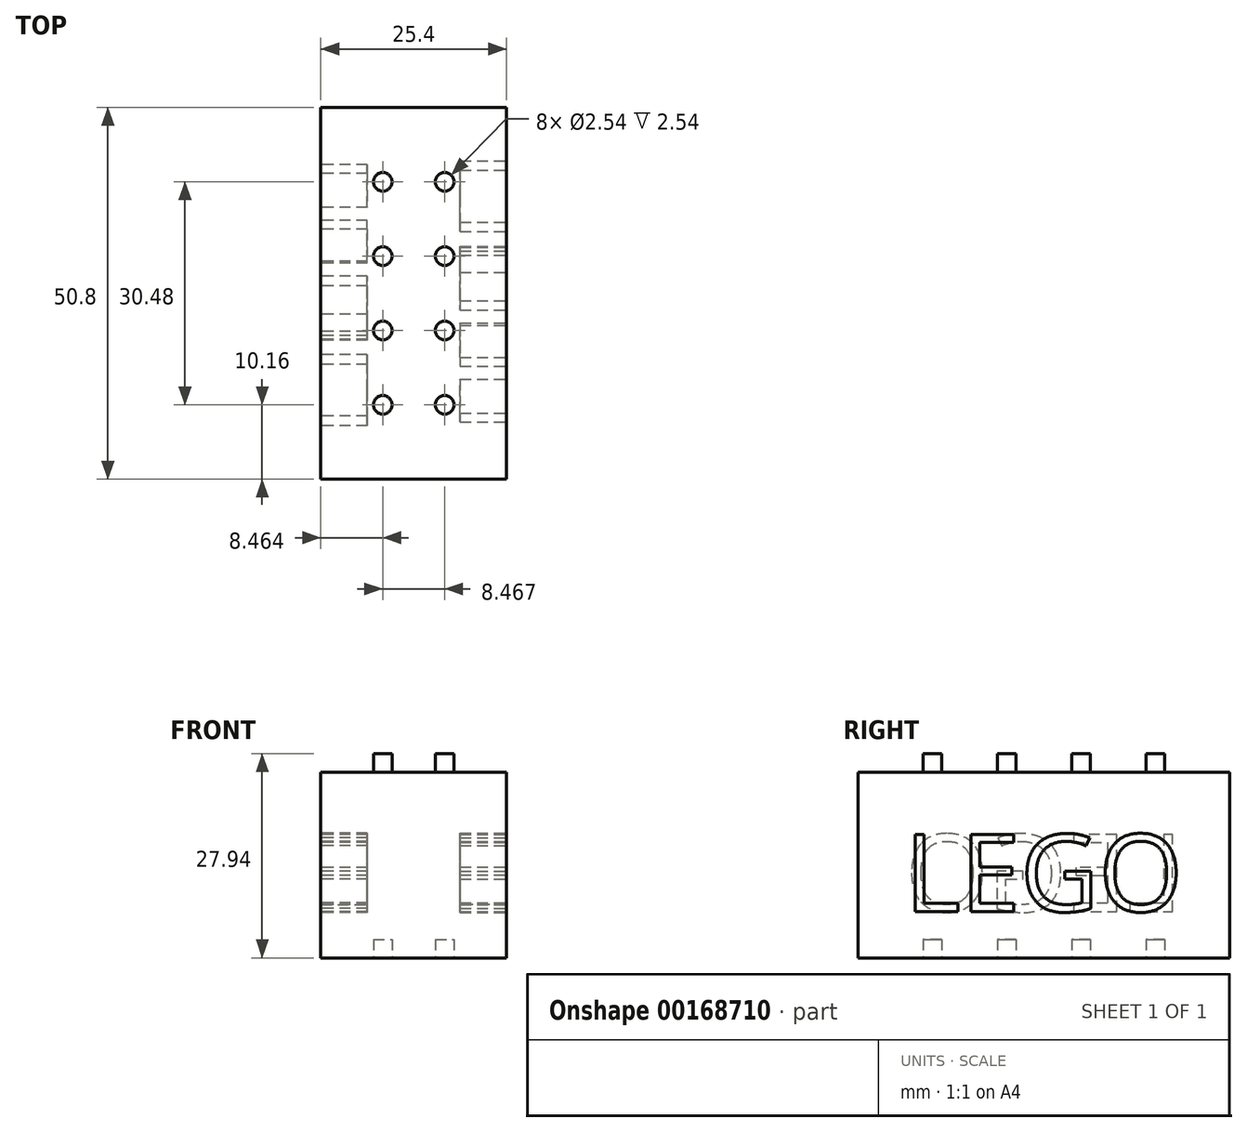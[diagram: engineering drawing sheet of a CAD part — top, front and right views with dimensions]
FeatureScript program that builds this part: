
annotation { "Feature Type Name" : "Feature", "Feature Type Description" : "" }
export const myFeature = defineFeature(function(context is Context, id is Id, definition is map)
    precondition{}
    {
        {
            var Q0;
            Q0=qCreatedBy(makeId("Top.planeOp"),FACE);
            var sketch = newSketch(context, id + "F0", { "sketchPlane" : qUnion([Q0])});
            skLineSegment(sketch, "E0.bottom", {"start": v(12.7, -25.4) * mm, "end": v(-12.7, -25.4) * mm});
            skLineSegment(sketch, "E0.top", {"start": v(12.7, 25.4) * mm, "end": v(-12.7, 25.4) * mm});
            skLineSegment(sketch, "E0.right", {"start": v(-12.7, -25.4) * mm, "end": v(-12.7, 25.4) * mm});
            skLineSegment(sketch, "E1", {"start": v(12.7, 25.4) * mm, "end": v(12.7, -25.4) * mm});
            skSolve(sketch);
        }
        {
            var Q0;
            Q0 = qSketchRegion(id + "F0", true);
            extrude(context, id + "F1", {"entities" : qUnion([Q0]), "depth" : 25.4 * mm});
        }
        {
            var Q0;
            Q0=makeQuery(id+"F1.opExtrude","CAP_FACE",FACE,{"disambiguationData":[OSD([sQuery(id+"F0.wireOp",EDGE,"E0.bottom"),sQuery(id+"F0.wireOp",EDGE,"E0.top"),sQuery(id+"F0.wireOp",EDGE,"E0.right"),sQuery(id+"F0.wireOp",EDGE,"E1")])],"isStart":true});
            var sketch = newSketch(context, id + "F2", { "sketchPlane" : qUnion([Q0])});
            skLineSegment(sketch, "E2", {"start": v(-12.7, 15.24) * mm, "end": v(12.7, 15.24) * mm, "construction": true});
            skLineSegment(sketch, "E3", {"start": v(-12.7, 5.08) * mm, "end": v(12.7, 5.08) * mm, "construction": true});
            skLineSegment(sketch, "E4", {"start": v(-12.7, -5.08) * mm, "end": v(12.7, -5.08) * mm, "construction": true});
            skLineSegment(sketch, "E5", {"start": v(-12.7, -15.24) * mm, "end": v(12.7, -15.24) * mm, "construction": true});
            skLineSegment(sketch, "E6", {"start": v(-4.24, 25.4) * mm, "end": v(-4.24, -25.4) * mm, "construction": true});
            skLineSegment(sketch, "E7", {"start": v(4.23, 25.4) * mm, "end": v(4.23, -25.4) * mm, "construction": true});
            skCircle(sketch, "E8", {"center": v(-4.24, 15.24) * mm, "radius": 1.27 * mm});
            skCircle(sketch, "E9", {"center": v(4.23, 15.24) * mm, "radius": 1.27 * mm});
            skCircle(sketch, "E10", {"center": v(-4.24, 5.08) * mm, "radius": 1.27 * mm});
            skCircle(sketch, "E11", {"center": v(4.23, 5.08) * mm, "radius": 1.27 * mm});
            skCircle(sketch, "E12", {"center": v(-4.24, -5.08) * mm, "radius": 1.27 * mm});
            skCircle(sketch, "E13", {"center": v(4.23, -5.08) * mm, "radius": 1.27 * mm});
            skCircle(sketch, "E14", {"center": v(-4.24, -15.24) * mm, "radius": 1.27 * mm});
            skCircle(sketch, "E15", {"center": v(4.23, -15.24) * mm, "radius": 1.27 * mm});
            skSolve(sketch);
        }
        {
            var Q0;
            Q0 = qSketchRegion(id + "F2", true);
            extrude(context, id + "F3", {"entities" : qUnion([Q0]), "operationType" : NewBodyOperationType.REMOVE, "oppositeDirection" : true, "depth" : 2.54 * mm});
        }
        {
            var Q0;
            Q0=makeQuery(id+"F1.opExtrude","CAP_FACE",FACE,{"disambiguationData":[OSD([sQuery(id+"F0.wireOp",EDGE,"E0.bottom"),sQuery(id+"F0.wireOp",EDGE,"E0.top"),sQuery(id+"F0.wireOp",EDGE,"E0.right"),sQuery(id+"F0.wireOp",EDGE,"E1")])],"isStart":false});
            var sketch = newSketch(context, id + "F4", { "sketchPlane" : qUnion([Q0])});
            skLineSegment(sketch, "E16", {"start": v(-12.79, 15.24) * mm, "end": v(12.61, 15.24) * mm, "construction": true});
            skLineSegment(sketch, "E17", {"start": v(-12.7, 5.08) * mm, "end": v(12.7, 5.08) * mm, "construction": true});
            skLineSegment(sketch, "E18", {"start": v(-12.7, -5.08) * mm, "end": v(12.7, -5.08) * mm, "construction": true});
            skLineSegment(sketch, "E19", {"start": v(-12.7, -15.24) * mm, "end": v(12.7, -15.24) * mm, "construction": true});
            skLineSegment(sketch, "E20", {"start": v(-4.23, 25.4) * mm, "end": v(-4.23, -25.4) * mm, "construction": true});
            skLineSegment(sketch, "E21", {"start": v(4.23, 25.4) * mm, "end": v(4.23, -25.4) * mm, "construction": true});
            skCircle(sketch, "E22", {"center": v(-4.23, 15.24) * mm, "radius": 1.27 * mm});
            skCircle(sketch, "E23", {"center": v(4.23, 15.24) * mm, "radius": 1.27 * mm});
            skCircle(sketch, "E24", {"center": v(-4.23, 5.08) * mm, "radius": 1.27 * mm});
            skCircle(sketch, "E25", {"center": v(4.23, 5.08) * mm, "radius": 1.27 * mm});
            skCircle(sketch, "E26", {"center": v(-4.23, -5.08) * mm, "radius": 1.27 * mm});
            skCircle(sketch, "E27", {"center": v(4.23, -5.08) * mm, "radius": 1.27 * mm});
            skCircle(sketch, "E28", {"center": v(-4.23, -15.24) * mm, "radius": 1.27 * mm});
            skCircle(sketch, "E29", {"center": v(4.23, -15.24) * mm, "radius": 1.27 * mm});
            skSolve(sketch);
        }
        {
            var Q0;
            Q0 = qSketchRegion(id + "F4", true);
            extrude(context, id + "F5", {"entities" : qUnion([Q0]), "operationType" : NewBodyOperationType.ADD, "depth" : 2.54 * mm});
        }
        {
            var Q0;
            Q0=makeQuery(id+"F1.opExtrude","SWEPT_FACE",FACE,{"disambiguationData":[OSD([sQuery(id+"F0.wireOp",EDGE,"E1")])]});
            var sketch = newSketch(context, id + "F6", { "sketchPlane" : qUnion([Q0])});
            skSolve(sketch);
        }
        {
            var Q0;
            Q0=makeQuery(id+"F1.opExtrude","SWEPT_FACE",FACE,{"disambiguationData":[OSD([sQuery(id+"F0.wireOp",EDGE,"E0.right")])]});
            var sketch = newSketch(context, id + "F7", { "sketchPlane" : qUnion([Q0])});
            skText(sketch, "E30", { "text": "LEGO\n", "fontName": "OpenSans-Regular.ttf"});
            const initialGuessF7  = {"E30": [-0.01905, 0.00635, 1, 0, 0.0106]};
            skSetInitialGuess(sketch, initialGuessF7);
            skSolve(sketch);
        }
        {
            var Q0;
            {var subQ0=sQuery(id+"F0.wireOp",EDGE,"E1");Q0=makeQuery(id+"F6.imprint","IMPRINT",FACE,{"disambiguationData":[TD([[makeQuery(id+"F6.imprint","IMPRINT",EDGE,{"derivedFrom":makeQuery(id+"F1.opExtrude","CAP_EDGE",EDGE,{"disambiguationData":[OSD([subQ0])],"isStart":true})}),-1.0]])]});}
            var sketch = newSketch(context, id + "F8", { "sketchPlane" : qUnion([Q0])});
            skText(sketch, "E31", { "text": "LEGO\n", "fontName": "OpenSans-Regular.ttf"});
            const initialGuessF8  = {"E31": [-0.01905, 0.00635, 1, 0, 0.01061]};
            skSetInitialGuess(sketch, initialGuessF8);
            skSolve(sketch);
        }
        {
            var Q0;
            Q0 = qSketchRegion(id + "F8", true);
            extrude(context, id + "F9", {"entities" : qUnion([Q0]), "operationType" : NewBodyOperationType.REMOVE, "oppositeDirection" : true, "depth" : 6.35 * mm});
        }
        {
            var Q0;
            Q0 = qSketchRegion(id + "F7", true);
            extrude(context, id + "F10", {"entities" : qUnion([Q0]), "operationType" : NewBodyOperationType.REMOVE, "oppositeDirection" : true, "depth" : 6.35 * mm});
        }
    });
